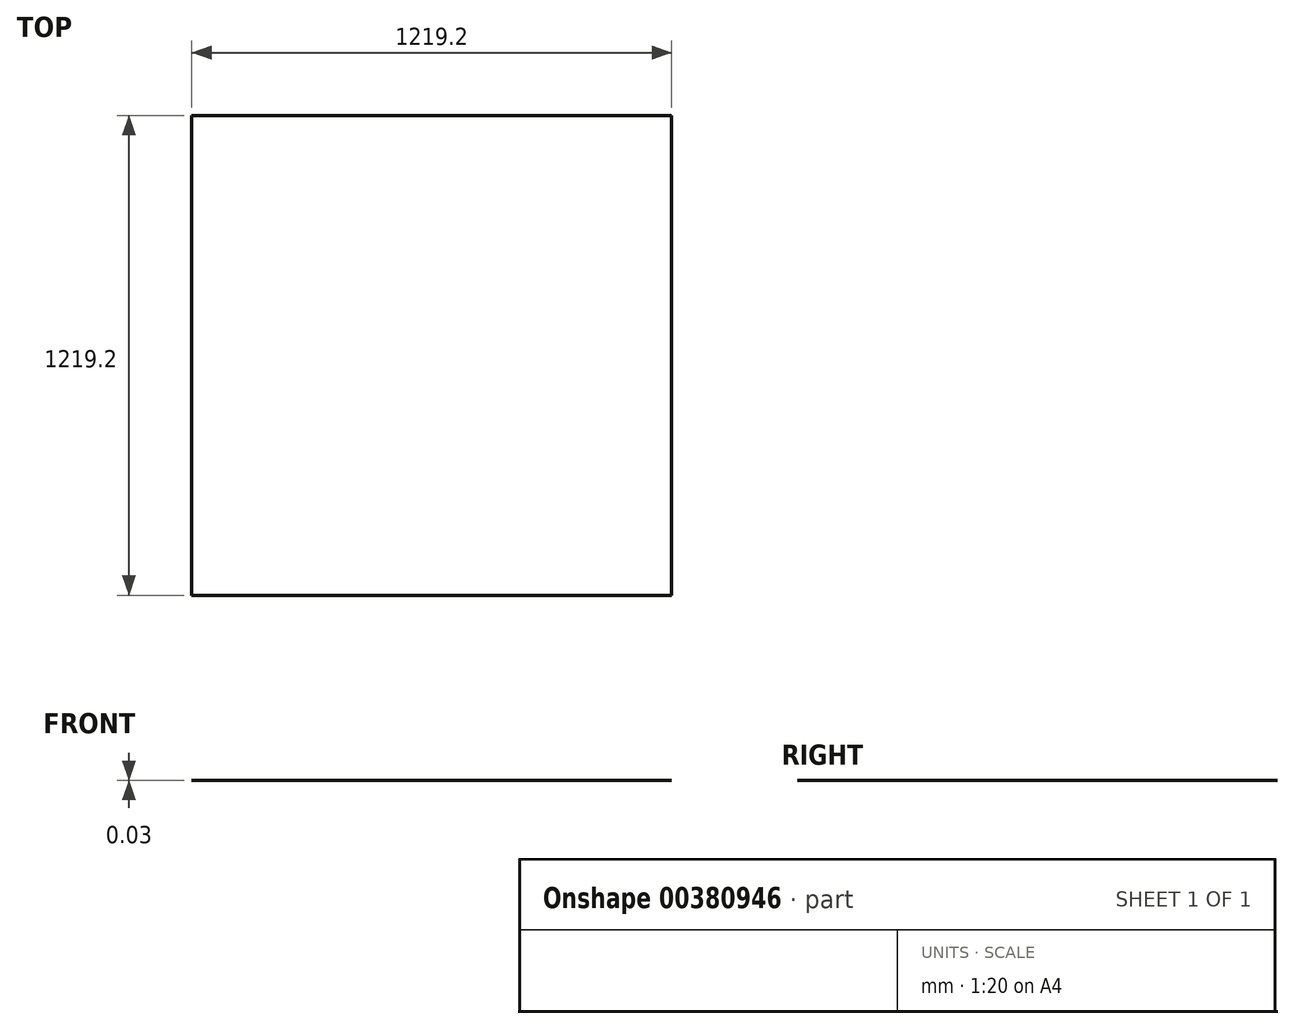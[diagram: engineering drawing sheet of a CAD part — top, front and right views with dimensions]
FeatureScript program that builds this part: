
annotation { "Feature Type Name" : "Feature", "Feature Type Description" : "" }
export const myFeature = defineFeature(function(context is Context, id is Id, definition is map)
    precondition{}
    {
        {
            var Q0;
            Q0=qCreatedBy(makeId("Top.planeOp"),FACE);
            var sketch = newSketch(context, id + "F0", { "sketchPlane" : qUnion([Q0])});
            skLineSegment(sketch, "E0.bottom", {"start": v(609.6, 609.6) * mm, "end": v(-609.6, 609.6) * mm});
            skLineSegment(sketch, "E0.top", {"start": v(609.6, -609.6) * mm, "end": v(-609.6, -609.6) * mm});
            skLineSegment(sketch, "E0.left", {"start": v(609.6, 609.6) * mm, "end": v(609.6, -609.6) * mm});
            skLineSegment(sketch, "E0.right", {"start": v(-609.6, 609.6) * mm, "end": v(-609.6, -609.6) * mm});
            skPoint(sketch, "E0.middle", {"position": v(0, 0) * mm});
            skSolve(sketch);
        }
        {
            var Q0;
            Q0 = qSketchRegion(id + "F0", true);
            extrude(context, id + "F1", {"entities" : qUnion([Q0]), "depth" : 0.03 * mm});
        }
    });
